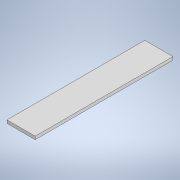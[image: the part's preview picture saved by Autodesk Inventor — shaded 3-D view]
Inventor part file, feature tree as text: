
AUTODESK INVENTOR PART (.ipt)
format: ipt  version: 2020 (Build 240168000, 168)  size: 91,648 bytes
history: native  units: mm
features: extrude x1, sketch x1
ambient origin geometry x8: Origin, YZ Plane, XZ Plane, XY Plane, X Axis, Y Axis, Z Axis, Center Point
bodies: Solide1 (feature_tree)
feature tree (2):
  extrude  "Extrusion1"  Depth=978.0mm
  sketch  "Esquisse1"
